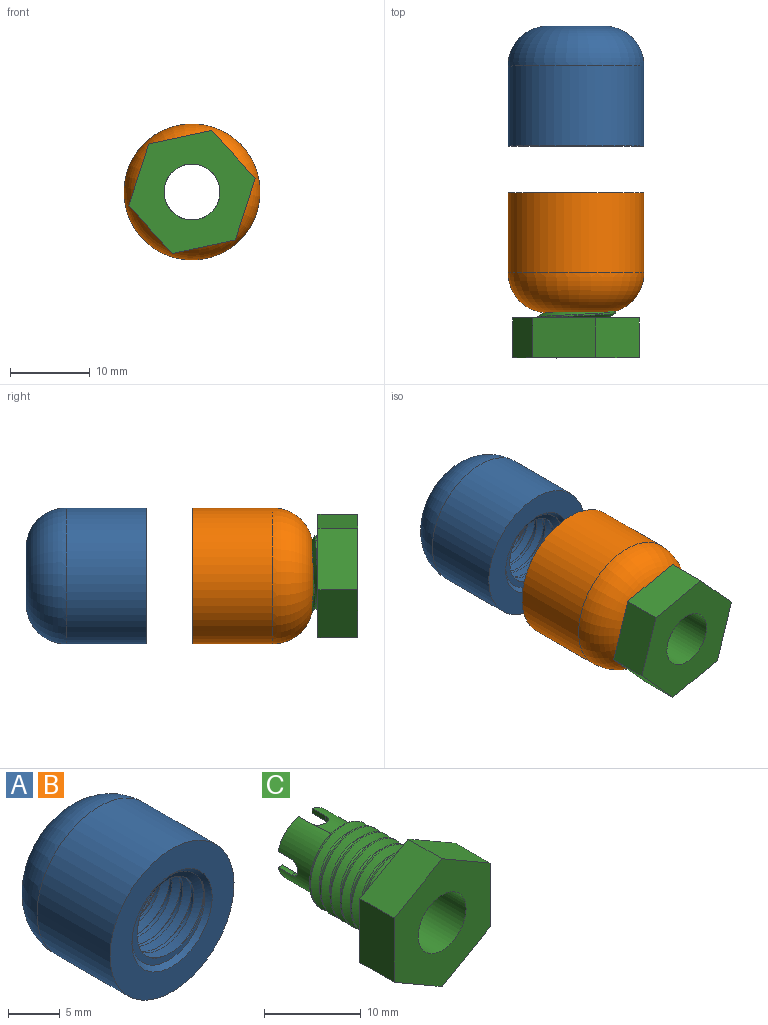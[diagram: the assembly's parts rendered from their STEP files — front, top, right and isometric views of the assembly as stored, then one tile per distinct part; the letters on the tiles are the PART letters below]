
ASSEMBLY  parts=3 mates=2
PART A: 14 faces, bbox 17.4x15.5x17.4 mm
  f0: bspline ~11.69x10.12mm, area 118.7mm2, adj f2,f3,f7,f8,f9
  f1: bspline ~11.69x10.12mm, area 118.9mm2, adj f2,f3,f7,f8,f9
  f2: bspline ~11.85x10.26mm, area 30.2mm2, adj f0,f1,f7,f9
  f3: cylinder r=4.25mm len=8.5mm, axis (0,1,0), area 43.8mm2, adj f0,f1,f8,f9
  f4: cylinder r=8.5mm len=17mm, axis (0,-1,0), area 534.1mm2, adj f5,f13
  f5: plane 17x17mm, normal (0,-1,0), area 131.9mm2, adj f4,f6
  f6: cone r=5mm half-angle=45deg, axis (0,-1,0), area 23.3mm2, adj f5,f7,f8
  f7: plane 3.77x3.71mm, normal (0,1,0), area 0.4mm2, adj f0,f1,f2,f6
  f8: plane 10.37x10.37mm, normal (0,-1,0), area 11.9mm2, adj f0,f1,f3,f6
  f9: plane 11.43x11.43mm, normal (0,1,0), area 28mm2, adj f0,f1,f2,f3,f10
  f10: cylinder r=5.5mm len=11mm, axis (0,1,0), area 87.6mm2, adj f9,f12
  f11: cylinder r=3.5mm len=7mm, axis (0,1,0), area 44mm2, adj f12,f13
  f12: cone r=5.5mm half-angle=30deg, axis (0,-1,0), area 113.1mm2, adj f10,f11
  f13: torus R=3.5mm, axis (0,-1,0), area 329.8mm2, adj f4,f11
PART B: same geometry as A
PART C: 32 faces, bbox 14.4x20.4x16.6 mm
  f0: cylinder r=3.5mm len=20mm, axis (0,-1,0), area 419.5mm2, adj f2,f3,f4,f13,f19,f20,f21,f22
  f1: cylinder r=4.1mm len=8.2mm, axis (0,-1,0), area 108.6mm2, adj f2,f3,f4,f5,f19,f20,f21,f22
  f2: plane 2.98x2.98mm, normal (0,1,0), area 2.4mm2, adj f0,f1,f21,f23
  f3: plane 2.98x2.98mm, normal (0,1,0), area 2.4mm2, adj f0,f1,f20,f26
  f4: plane 2.98x2.98mm, normal (0,1,0), area 2.4mm2, adj f0,f1,f25,f27
  f5: plane 8.56x8.42mm, normal (0,1,0), area 3.1mm2, adj f1,f15,f16,f17,f18
  f6: cylinder r=5mm len=10mm, axis (0,-1,0), area 54mm2, adj f14,f16,f17,f18
  f7: plane 7x5mm, normal (0.5,0,-0.87), area 40.4mm2, adj f8,f12,f13,f14
  f8: plane 8.08x5mm, normal (1,0,0), area 40.4mm2, adj f7,f9,f13,f14
  f9: plane 7x5mm, normal (0.5,0,0.87), area 40.4mm2, adj f8,f10,f13,f14
  f10: plane 7x5mm, normal (-0.5,0,0.87), area 40.4mm2, adj f9,f11,f13,f14
  f11: plane 8.08x5mm, normal (-1,0,0), area 40.4mm2, adj f10,f12,f13,f14
  f12: plane 7x5mm, normal (-0.5,0,-0.87), area 40.4mm2, adj f7,f11,f13,f14
  f13: plane 16.17x14mm, normal (0,-1,0), area 131.3mm2, adj f0,f7,f8,f9,f10,f11,f12
  f14: plane 16.58x14.42mm, normal (0,1,0), area 105mm2, adj f6,f7,f8,f9,f10,f11,f12,f15
  f15: bspline ~11.13x9.67mm, area 73.4mm2, adj f5,f14,f16,f17
  f16: bspline ~11.55x11.22mm, area 176.3mm2, adj f5,f6,f14,f15,f18
  f17: bspline ~11.55x10.72mm, area 176.2mm2, adj f5,f6,f14,f15,f18
  f18: cone r=5mm half-angle=63.4deg, axis (0,-1,0), area 9.9mm2, adj f5,f6,f16,f17
  f19: plane 2.98x2.98mm, normal (0,1,0), area 2.4mm2, adj f0,f1,f22,f24
  f20: plane 2x0.62mm, normal (-1,0,0), area 1.2mm2, adj f0,f1,f3,f30
  f21: plane 2x0.62mm, normal (1,0,0), area 1.2mm2, adj f0,f1,f2,f30
  f22: plane 2x0.62mm, normal (0,0,1), area 1.2mm2, adj f0,f1,f19,f31
  f23: plane 2x0.62mm, normal (0,0,-1), area 1.2mm2, adj f0,f1,f2,f31
  f24: plane 2x0.62mm, normal (1,0,0), area 1.2mm2, adj f0,f1,f19,f28
  f25: plane 2x0.62mm, normal (-1,0,0), area 1.2mm2, adj f0,f1,f4,f28
  f26: plane 2x0.62mm, normal (0,0,-1), area 1.2mm2, adj f0,f1,f3,f29
  f27: plane 2x0.62mm, normal (0,0,1), area 1.2mm2, adj f0,f1,f4,f29
  f28: cylinder r=1mm len=2mm, axis (0,0,-1), area 1.9mm2, adj f0,f1,f24,f25
  f29: cylinder r=1mm len=2mm, axis (1,0,0), area 1.9mm2, adj f0,f1,f26,f27
  f30: cylinder r=1mm len=2mm, axis (0,0,1), area 1.9mm2, adj f0,f1,f20,f21
  f31: cylinder r=1mm len=2mm, axis (-1,0,0), area 1.9mm2, adj f0,f1,f22,f23
PLACE A rot(axis=(0,-1,0),8.3deg) t=(-8.24,28.32,4.17)mm
PLACE B rot(axis=(0.83,0,0.55),180deg) t=(-8.24,22.45,4.17)mm
PLACE C rot(axis=(0,1,0),77.8deg) t=(-8.24,6.82,4.17)mm fixed
MATE cylindrical B.f3 <-> C.f0  axis (0,1,0) through (-8.24,22.45,4.17)mm
MATE cylindrical C.f0 <-> A.f3  axis (0,-1,0) through (-8.24,1.67,4.17)mm
